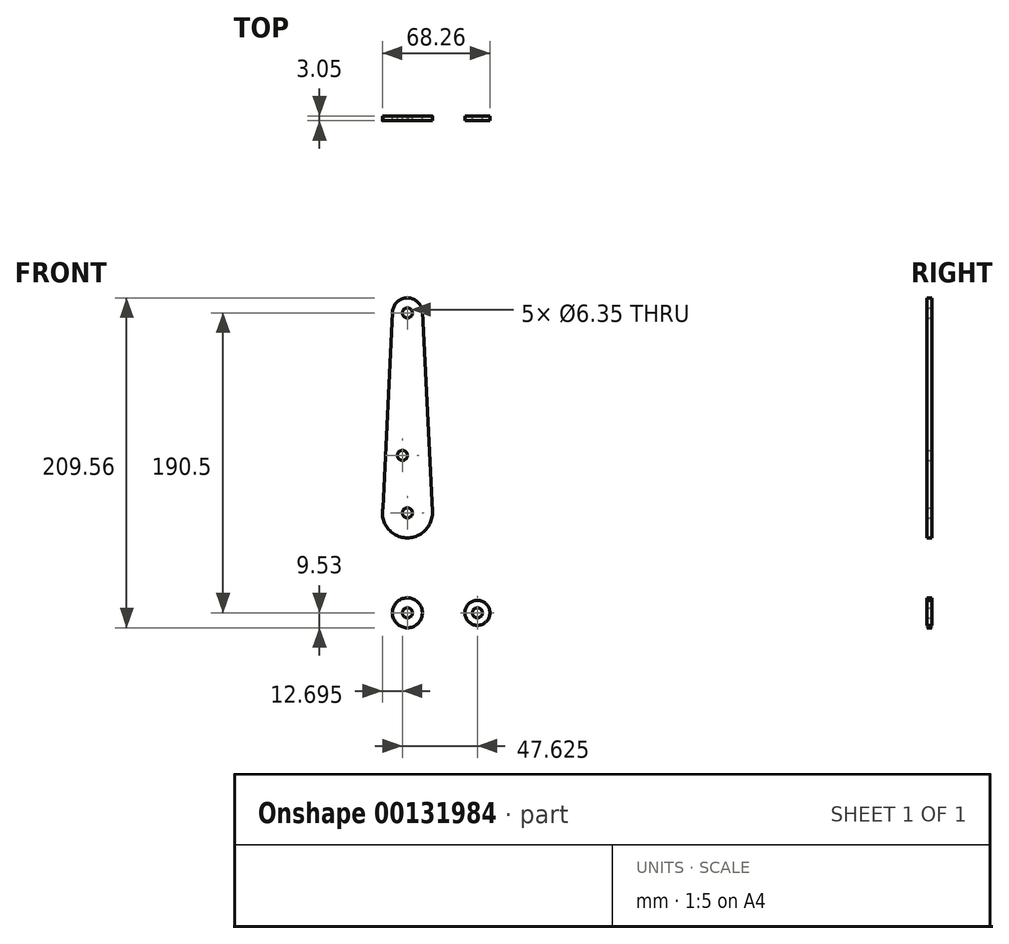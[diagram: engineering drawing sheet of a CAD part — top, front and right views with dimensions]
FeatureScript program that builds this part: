
annotation { "Feature Type Name" : "Feature", "Feature Type Description" : "" }
export const myFeature = defineFeature(function(context is Context, id is Id, definition is map)
    precondition{}
    {
        {
            var Q0;
            Q0=qCreatedBy(makeId("Front.planeOp"),FACE);
            var sketch = newSketch(context, id + "F0", { "sketchPlane" : qUnion([Q0])});
            skCircle(sketch, "E0", {"center": v(0, 0) * mm, "radius": 9.53 * mm});
            skCircle(sketch, "E1", {"center": v(0, 63.5) * mm, "radius": 15.88 * mm});
            skCircle(sketch, "E2", {"center": v(0, 190.5) * mm, "radius": 9.53 * mm});
            skCircle(sketch, "E3", {"center": v(44.45, 0) * mm, "radius": 7.94 * mm});
            skLineSegment(sketch, "E4", {"start": v(0, 190.5) * mm, "end": v(0, 63.5) * mm, "construction": true});
            skLineSegment(sketch, "E5", {"start": v(0, 0) * mm, "end": v(0, 63.5) * mm, "construction": true});
            skLineSegment(sketch, "E6", {"start": v(0, 0) * mm, "end": v(44.45, 0) * mm, "construction": true});
            skLineSegment(sketch, "E7", {"start": v(-9.51, 190.96) * mm, "end": v(-15.8, 61.91) * mm});
            skLineSegment(sketch, "E8", {"start": v(-15.8, 61.91) * mm, "end": v(-9.57, 0) * mm});
            skLineSegment(sketch, "E9", {"start": v(9.51, 190.98) * mm, "end": v(15.86, 64.3) * mm});
            skLineSegment(sketch, "E10", {"start": v(0, -9.53) * mm, "end": v(44.73, -7.93) * mm});
            skCircle(sketch, "E11", {"center": v(0, 190.5) * mm, "radius": 3.18 * mm});
            skCircle(sketch, "E12", {"center": v(-3.17, 100.03) * mm, "radius": 3.18 * mm});
            skCircle(sketch, "E13", {"center": v(0, 63.5) * mm, "radius": 3.18 * mm});
            skCircle(sketch, "E14", {"center": v(0, 0) * mm, "radius": 3.18 * mm});
            skCircle(sketch, "E15", {"center": v(44.45, 0) * mm, "radius": 3.18 * mm});
            skPoint(sketch, "E16.newPointB", {"position": v(0, 0.5) * mm});
            skLineSegment(sketch, "E17", {"start": v(15.8, 61.9) * mm, "end": v(11.3, 17.6) * mm});
            skLineSegment(sketch, "E18", {"start": v(18.93, 8.85) * mm, "end": v(44.73, 7.93) * mm});
            skPoint(sketch, "E19.newPointB", {"position": v(0, 9.53) * mm});
            skArc(sketch, "E19.filletArc", {"start": v(11.3, 17.6) * mm, "mid": v(13.22, 11.57) * mm, "end": v(18.93, 8.85) * mm});
            skSolve(sketch);
        }
        {
            var Q0;
            {var subQ0=sQuery(id+"F0.wireOp",EDGE,"E10");var subQ1=sQuery(id+"F0.wireOp",EDGE,"E0");var subQ2=makeQuery(id+"F0.imprint","INTERSECT",VERTEX,{"disambiguationData":[OD(0.0)],"derivedFrom":[subQ1,subQ0]});Q0=makeQuery(id+"F0.imprint","IMPRINT",FACE,{"disambiguationData":[TD([[makeQuery(id+"F0.imprint","IMPRINT",EDGE,{"disambiguationData":[TD([[subQ2,-1.0]])],"derivedFrom":subQ1}),1.0]])]});}
            var Q1;
            {var subQ0=sQuery(id+"F0.wireOp",EDGE,"E7");var subQ1=sQuery(id+"F0.wireOp",EDGE,"E1");var subQ2=makeQuery(id+"F0.imprint","INTERSECT",VERTEX,{"disambiguationData":[OD(0.0)],"derivedFrom":[subQ1,subQ0]});Q1=makeQuery(id+"F0.imprint","IMPRINT",FACE,{"disambiguationData":[TD([[makeQuery(id+"F0.imprint","IMPRINT",EDGE,{"disambiguationData":[TD([[subQ2,1.0]])],"derivedFrom":subQ1}),1.0]])]});}
            var Q2;
            Q2=makeQuery(id+"F0.imprint","IMPRINT",FACE,{"disambiguationData":[TD([[makeQuery(id+"F0.imprint","IMPRINT",EDGE,{"derivedFrom":sQuery(id+"F0.wireOp",EDGE,"E15")}),-1.0]])]});
            var Q3;
            Q3=makeQuery(id+"F0.imprint","IMPRINT",FACE,{"disambiguationData":[TD([[makeQuery(id+"F0.imprint","IMPRINT",EDGE,{"derivedFrom":sQuery(id+"F0.wireOp",EDGE,"E14")}),-1.0]])]});
            var Q4;
            Q4=makeQuery(id+"F0.imprint","IMPRINT",FACE,{"disambiguationData":[TD([[makeQuery(id+"F0.imprint","IMPRINT",EDGE,{"derivedFrom":sQuery(id+"F0.wireOp",EDGE,"E11")}),-1.0]])]});
            var Q5;
            Q5=makeQuery(id+"F0.imprint","IMPRINT",FACE,{"disambiguationData":[TD([[makeQuery(id+"F0.imprint","IMPRINT",EDGE,{"derivedFrom":sQuery(id+"F0.wireOp",EDGE,"E13")}),-1.0]])]});
            var Q6;
            {var subQ0=sQuery(id+"F0.wireOp",EDGE,"E9");Q6=makeQuery(id+"F0.imprint","IMPRINT",FACE,{"disambiguationData":[TD([[makeQuery(id+"F0.imprint","IMPRINT",EDGE,{"derivedFrom":subQ0}),-1.0]])]});}
            extrude(context, id + "F1", {"entities" : qUnion([Q0, Q1, Q2, Q3, Q4, Q5, Q6]), "depth" : 3.05 * mm});
        }
    });
